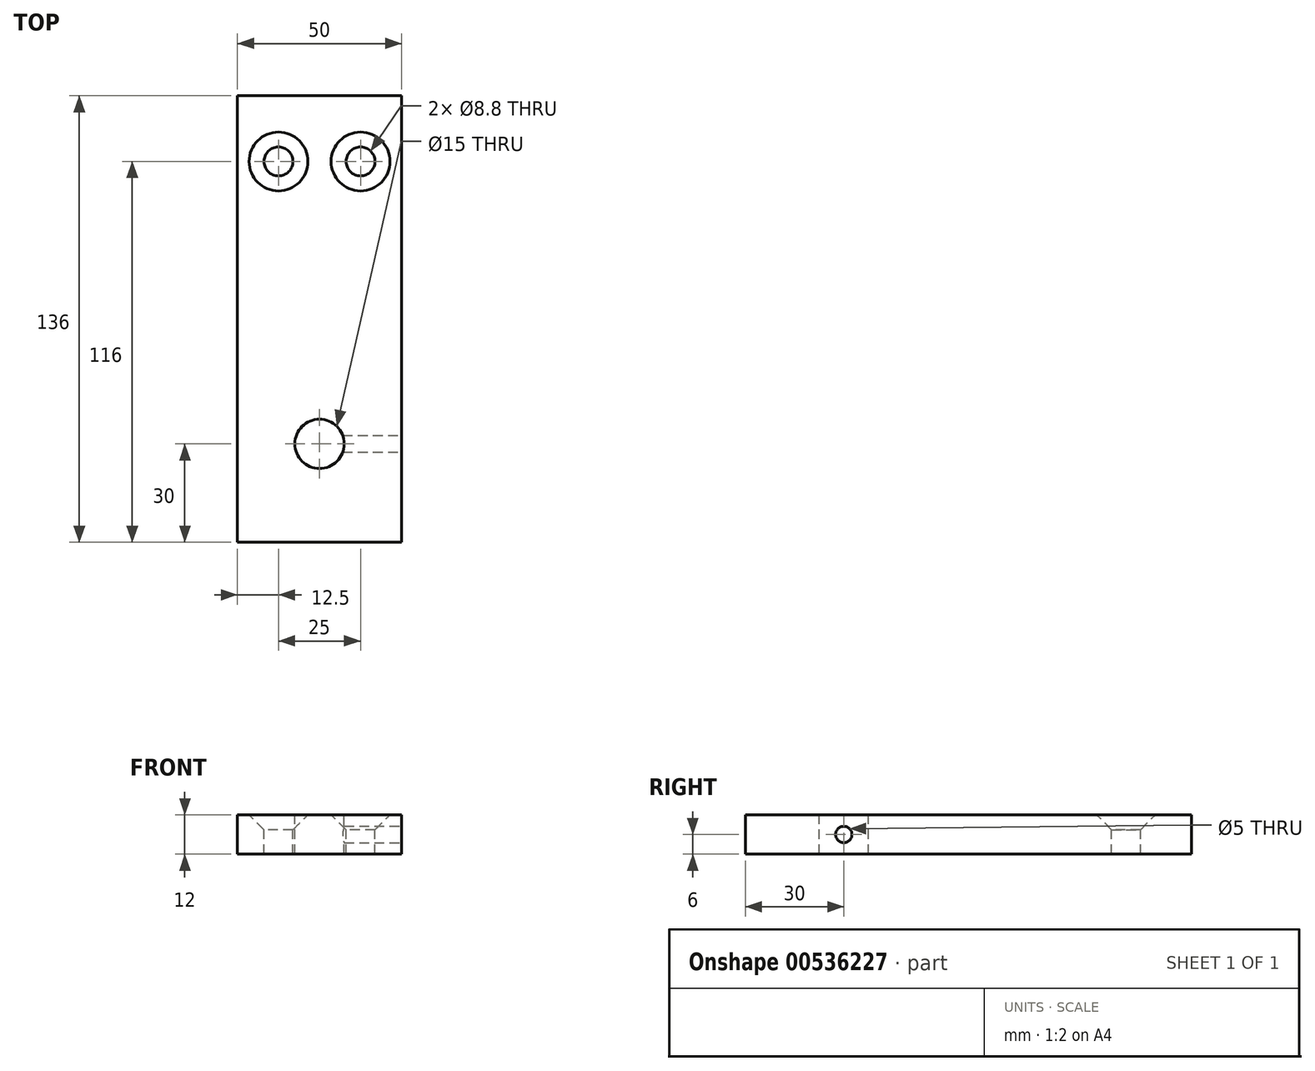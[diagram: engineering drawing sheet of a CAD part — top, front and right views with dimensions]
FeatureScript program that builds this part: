
annotation { "Feature Type Name" : "Feature", "Feature Type Description" : "" }
export const myFeature = defineFeature(function(context is Context, id is Id, definition is map)
    precondition{}
    {
        {
            var Q0;
            Q0=qCreatedBy(makeId("Top.planeOp"),FACE);
            var sketch = newSketch(context, id + "F0", { "sketchPlane" : qUnion([Q0])});
            skLineSegment(sketch, "E0.bottom", {"start": v(-25, 68) * mm, "end": v(25, 68) * mm});
            skLineSegment(sketch, "E0.top", {"start": v(-25, -68) * mm, "end": v(25, -68) * mm});
            skLineSegment(sketch, "E0.left", {"start": v(-25, 68) * mm, "end": v(-25, -68) * mm});
            skLineSegment(sketch, "E0.right", {"start": v(25, 68) * mm, "end": v(25, -68) * mm});
            skPoint(sketch, "E0.middle", {"position": v(0, 0) * mm});
            skPoint(sketch, "E1", {"position": v(0, -38) * mm});
            skSolve(sketch);
        }
        {
            var Q0;
            Q0 = qSketchRegion(id + "F0", true);
            extrude(context, id + "F1", {"entities" : qUnion([Q0]), "oppositeDirection" : true, "depth" : 12 * mm, "offsetDistance" : 25 * mm});
        }
        {
            var Q0;
            Q0=makeQuery(id+"F1.opExtrude","CAP_FACE",FACE,{"disambiguationData":[OSD([sQuery(id+"F0.wireOp",EDGE,"E0.bottom"),sQuery(id+"F0.wireOp",EDGE,"E0.top"),sQuery(id+"F0.wireOp",EDGE,"E0.left"),sQuery(id+"F0.wireOp",EDGE,"E0.right")])],"isStart":true});
            var sketch = newSketch(context, id + "F2", { "sketchPlane" : qUnion([Q0])});
            skPoint(sketch, "E2", {"position": v(0, -38) * mm});
            skSolve(sketch);
        }
        {
            var Q0;
            Q0=sQuery(id+"F2.wireOp",VERTEX,"E2");
            var Q1;
            Q1=makeQuery(id+"F1.opExtrude","SWEPT_BODY",BODY,{"disambiguationData":[OSD([sQuery(id+"F0.wireOp",EDGE,"E0.bottom"),sQuery(id+"F0.wireOp",EDGE,"E0.top"),sQuery(id+"F0.wireOp",EDGE,"E0.left"),sQuery(id+"F0.wireOp",EDGE,"E0.right")])]});
            hole(context, id + "F3", {"style" : HoleStyle.SIMPLE, "endStyle" : HoleEndStyle.THROUGH, "holeDiameter" : 15 * mm, "isTappedThrough" : true, "tappedDepth" : 17 * mm, "tapClearance" : 3, "locations" : qUnion([Q0]), "scope" : qUnion([Q1])});
        }
        {
            var Q0;
            Q0=makeQuery(id+"F1.opExtrude","CAP_FACE",FACE,{"disambiguationData":[OSD([sQuery(id+"F0.wireOp",EDGE,"E0.bottom"),sQuery(id+"F0.wireOp",EDGE,"E0.top"),sQuery(id+"F0.wireOp",EDGE,"E0.left"),sQuery(id+"F0.wireOp",EDGE,"E0.right")])],"isStart":true});
            var sketch = newSketch(context, id + "F4", { "sketchPlane" : qUnion([Q0])});
            skLineSegment(sketch, "E3", {"start": v(0, 68) * mm, "end": v(0, -68) * mm});
            skPoint(sketch, "E4", {"position": v(-12.5, 48) * mm});
            skPoint(sketch, "E5", {"position": v(12.5, 48) * mm});
            skSolve(sketch);
        }
        {
            var Q0;
            Q0=sQuery(id+"F4.wireOp",VERTEX,"E5");
            var Q1;
            Q1=sQuery(id+"F4.wireOp",VERTEX,"E4");
            var Q2;
            Q2=makeQuery(id+"F1.opExtrude","SWEPT_BODY",BODY,{"disambiguationData":[OSD([sQuery(id+"F0.wireOp",EDGE,"E0.bottom"),sQuery(id+"F0.wireOp",EDGE,"E0.top"),sQuery(id+"F0.wireOp",EDGE,"E0.left"),sQuery(id+"F0.wireOp",EDGE,"E0.right")])]});
            hole(context, id + "F5", {"style" : HoleStyle.C_SINK, "endStyle" : HoleEndStyle.THROUGH, "standardTappedOrClearance" : lookupTablePath({ "standard" : "ISO", "fit" : "Normal", "size" : "M8", "type" : "Clearance" }), "standardBlindInLast" : lookupTablePath({ "fit" : "Standard", "standard" : "ISO", "size" : "M8", "type" : "Clearance" }), "holeDiameter" : 8.8 * mm, "cSinkDiameter" : 17.92 * mm, "cSinkAngle" : 90 * degree, "isTappedThrough" : true, "tappedDepth" : 17 * mm, "tapClearance" : 3, "locations" : qUnion([Q0, Q1]), "scope" : qUnion([Q2])});
        }
        {
            var Q0;
            Q0=makeQuery(id+"F1.opExtrude","SWEPT_FACE",FACE,{"disambiguationData":[OSD([sQuery(id+"F0.wireOp",EDGE,"E0.right")])]});
            var sketch = newSketch(context, id + "F6", { "sketchPlane" : qUnion([Q0])});
            skLineSegment(sketch, "E6", {"start": v(-68, -6) * mm, "end": v(68, -6) * mm});
            skPoint(sketch, "E7", {"position": v(-68, -6) * mm});
            skPoint(sketch, "E8", {"position": v(-38, -6) * mm});
            skSolve(sketch);
        }
        {
            var Q0;
            Q0=sQuery(id+"F6.wireOp",VERTEX,"E8");
            var Q1;
            Q1=makeQuery(id+"F1.opExtrude","SWEPT_BODY",BODY,{"disambiguationData":[OSD([sQuery(id+"F0.wireOp",EDGE,"E0.bottom"),sQuery(id+"F0.wireOp",EDGE,"E0.top"),sQuery(id+"F0.wireOp",EDGE,"E0.left"),sQuery(id+"F0.wireOp",EDGE,"E0.right")])]});
            hole(context, id + "F7", {"style" : HoleStyle.SIMPLE, "endStyle" : HoleEndStyle.BLIND, "standardTappedOrClearance" : lookupTablePath({ "standard" : "ISO", "engagement" : "75%", "pitch" : "1 mm", "size" : "M6", "type" : "Tapped" }), "standardBlindInLast" : lookupTablePath({ "standard" : "ISO", "engagement" : "75%", "pitch" : "1 mm", "size" : "M6", "type" : "Tapped" }), "holeDiameter" : 5 * mm, "showTappedDepth" : true, "holeDepth" : 20 * mm, "isTappedThrough" : true, "tappedDepth" : 17 * mm, "tapClearance" : 3, "locations" : qUnion([Q0]), "scope" : qUnion([Q1]), "majorDiameter" : 6 * mm});
        }
    });
